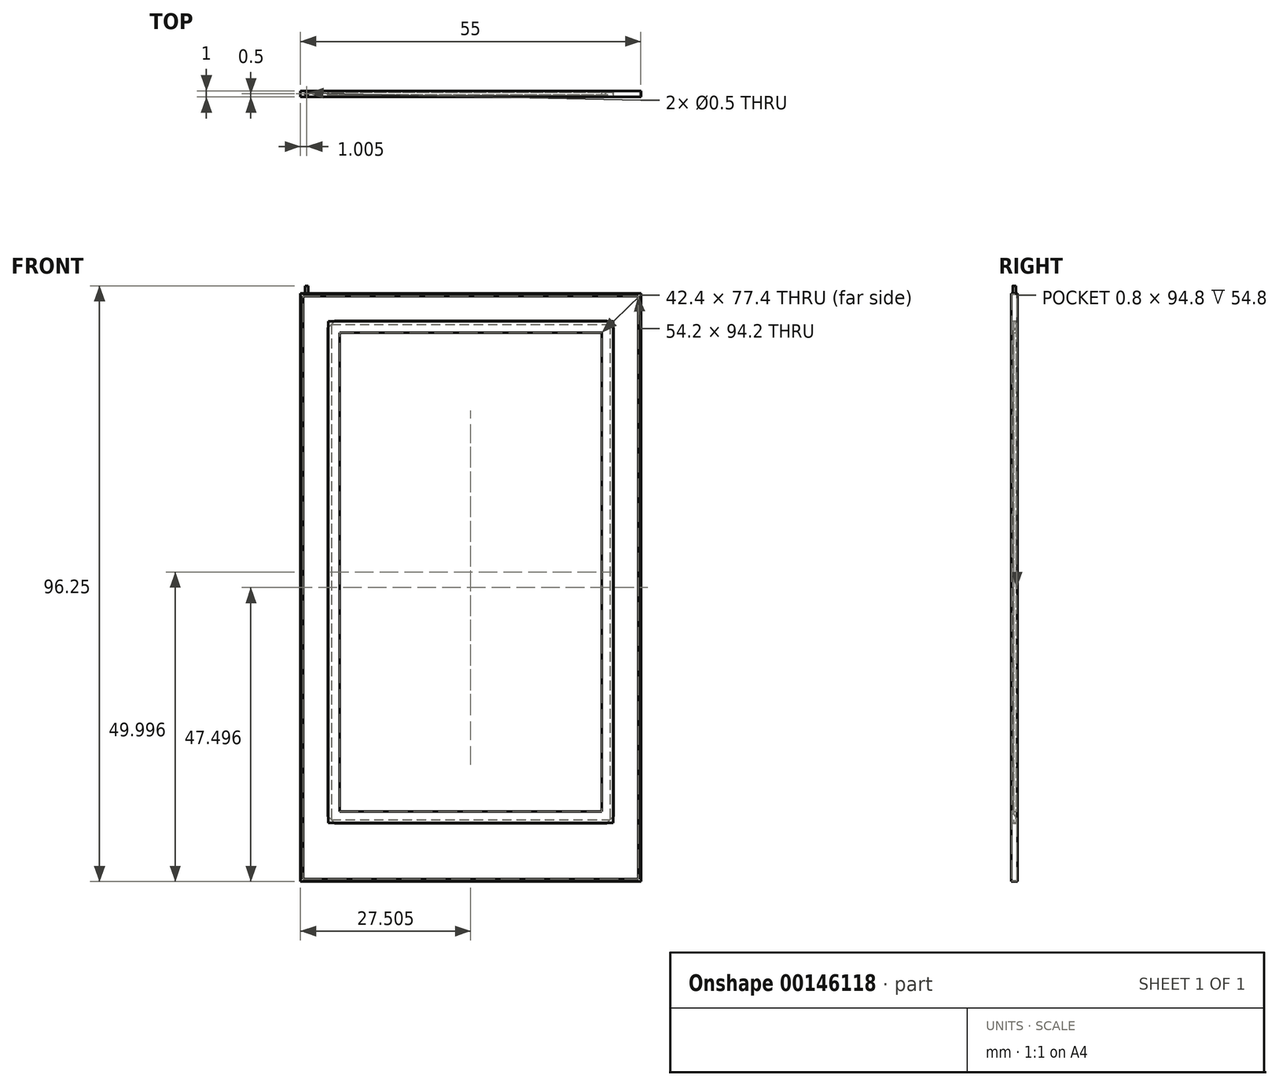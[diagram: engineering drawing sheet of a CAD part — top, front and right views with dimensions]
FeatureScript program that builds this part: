
annotation { "Feature Type Name" : "Feature", "Feature Type Description" : "" }
export const myFeature = defineFeature(function(context is Context, id is Id, definition is map)
    precondition{}
    {
        {
            var Q0;
            Q0=qCreatedBy(makeId("Front.planeOp"),FACE);
            var sketch = newSketch(context, id + "F0", { "sketchPlane" : qUnion([Q0])});
            skLineSegment(sketch, "E0.bottom", {"start": v(-18.52, 34.44) * mm, "end": v(38.48, 34.44) * mm});
            skLineSegment(sketch, "E0.top", {"start": v(-18.52, -62.56) * mm, "end": v(38.48, -62.56) * mm});
            skLineSegment(sketch, "E0.left", {"start": v(-18.52, 34.44) * mm, "end": v(-18.52, -62.56) * mm});
            skLineSegment(sketch, "E0.right", {"start": v(38.48, 34.44) * mm, "end": v(38.48, -62.56) * mm});
            skSolve(sketch);
        }
        {
            var Q0;
            Q0=makeQuery(id+"F0.imprint","IMPRINT",FACE,{"disambiguationData":[TD([[makeQuery(id+"F0.imprint","IMPRINT",EDGE,{"derivedFrom":sQuery(id+"F0.wireOp",EDGE,"E0.bottom")}),-1.0]])]});
            extrude(context, id + "F1", {"entities" : qUnion([Q0]), "depth" : .1 * mm});
        }
        {
            var Q0;
            Q0=makeQuery(id+"F1.opExtrude","CAP_FACE",FACE,{"disambiguationData":[OSD([sQuery(id+"F0.wireOp",EDGE,"E0.bottom"),sQuery(id+"F0.wireOp",EDGE,"E0.top"),sQuery(id+"F0.wireOp",EDGE,"E0.left"),sQuery(id+"F0.wireOp",EDGE,"E0.right")])],"isStart":false});
            var sketch = newSketch(context, id + "F2", { "sketchPlane" : qUnion([Q0])});
            skLineSegment(sketch, "E1.0", {"start": v(-18.22, 34.14) * mm, "end": v(38.18, 34.14) * mm});
            skLineSegment(sketch, "E1.1", {"start": v(-18.22, 34.14) * mm, "end": v(-18.22, -62.26) * mm});
            skLineSegment(sketch, "E1.2", {"start": v(-18.22, -62.26) * mm, "end": v(38.18, -62.26) * mm});
            skLineSegment(sketch, "E1.3", {"start": v(38.18, 34.14) * mm, "end": v(38.18, -62.26) * mm});
            skLineSegment(sketch, "E2.0", {"start": v(-17.52, 33.44) * mm, "end": v(-17.52, -61.56) * mm});
            skLineSegment(sketch, "E2.1", {"start": v(-17.52, 33.44) * mm, "end": v(37.48, 33.44) * mm});
            skLineSegment(sketch, "E2.2", {"start": v(37.48, 33.44) * mm, "end": v(37.48, -61.56) * mm});
            skLineSegment(sketch, "E2.3", {"start": v(-17.52, -61.56) * mm, "end": v(37.48, -61.56) * mm});
            skLineSegment(sketch, "E3", {"start": v(-17.52, 33.44) * mm, "end": v(-17.52, 34.44) * mm});
            skLineSegment(sketch, "E4", {"start": v(-17.52, 33.44) * mm, "end": v(-18.52, 33.44) * mm});
            skLineSegment(sketch, "E5.0", {"start": v(-16.52, 33.44) * mm, "end": v(-16.52, 34.14) * mm, "construction": true});
            skLineSegment(sketch, "E6", {"start": v(37.48, 33.44) * mm, "end": v(37.48, 34.44) * mm});
            skLineSegment(sketch, "E7", {"start": v(37.48, 33.44) * mm, "end": v(38.48, 33.44) * mm});
            skLineSegment(sketch, "E8", {"start": v(37.48, -61.56) * mm, "end": v(37.48, -62.56) * mm});
            skLineSegment(sketch, "E9", {"start": v(37.48, -61.56) * mm, "end": v(38.48, -61.56) * mm});
            skLineSegment(sketch, "E10", {"start": v(-17.52, -61.56) * mm, "end": v(-18.52, -61.56) * mm});
            skLineSegment(sketch, "E11", {"start": v(-17.52, -61.56) * mm, "end": v(-17.52, -62.56) * mm});
            skLineSegment(sketch, "E12", {"start": v(-16.52, -61.56) * mm, "end": v(-16.52, -62.26) * mm, "construction": true});
            skCircle(sketch, "E13", {"center": v(-16.52, -61.91) * mm, "radius": 0.25 * mm});
            skCircle(sketch, "E14", {"center": v(-16.52, 33.79) * mm, "radius": 0.25 * mm});
            skLineSegment(sketch, "E15.0", {"start": v(-17.42, 33.34) * mm, "end": v(37.38, 33.34) * mm});
            skLineSegment(sketch, "E15.1", {"start": v(-17.42, 33.34) * mm, "end": v(-17.42, -61.46) * mm});
            skLineSegment(sketch, "E15.2", {"start": v(-17.42, -61.46) * mm, "end": v(37.38, -61.46) * mm});
            skLineSegment(sketch, "E15.3", {"start": v(37.38, 33.34) * mm, "end": v(37.38, -61.46) * mm});
            skLineSegment(sketch, "E16.0", {"start": v(-17.52, -51.56) * mm, "end": v(-17.42, -51.56) * mm, "construction": true});
            skLineSegment(sketch, "E17.0", {"start": v(-12.52, 33.44) * mm, "end": v(-12.52, 33.34) * mm, "construction": true});
            skLineSegment(sketch, "E18.0", {"start": v(32.48, 33.44) * mm, "end": v(32.48, 33.34) * mm, "construction": true});
            skLineSegment(sketch, "E19.0", {"start": v(-17.52, 28.44) * mm, "end": v(-17.42, 28.44) * mm, "construction": true});
            skLineSegment(sketch, "E20.trimOffspring", {"start": v(-12.52, 28.44) * mm, "end": v(-12.52, -51.56) * mm, "construction": true});
            skLineSegment(sketch, "E21.trimOffspring", {"start": v(-12.52, 28.44) * mm, "end": v(32.48, 28.44) * mm, "construction": true});
            skLineSegment(sketch, "E22.trimOffspring", {"start": v(32.48, 28.44) * mm, "end": v(32.48, -51.56) * mm, "construction": true});
            skLineSegment(sketch, "E23.trimOffspring", {"start": v(37.38, 28.44) * mm, "end": v(37.48, 28.44) * mm, "construction": true});
            skLineSegment(sketch, "E24.trimOffspring", {"start": v(37.38, -51.56) * mm, "end": v(37.48, -51.56) * mm, "construction": true});
            skLineSegment(sketch, "E25.trimOffspring", {"start": v(32.48, -61.46) * mm, "end": v(32.48, -61.56) * mm, "construction": true});
            skLineSegment(sketch, "E26.trimOffspring", {"start": v(-12.52, -61.46) * mm, "end": v(-12.52, -61.56) * mm, "construction": true});
            skLineSegment(sketch, "E27.trimOffspring", {"start": v(-12.52, -51.56) * mm, "end": v(32.48, -51.56) * mm, "construction": true});
            skLineSegment(sketch, "E28.0", {"start": v(32.18, 28.14) * mm, "end": v(32.18, -51.26) * mm, "construction": true});
            skLineSegment(sketch, "E28.1", {"start": v(-12.22, 28.14) * mm, "end": v(32.18, 28.14) * mm, "construction": true});
            skLineSegment(sketch, "E28.2", {"start": v(-12.22, 28.14) * mm, "end": v(-12.22, -51.26) * mm, "construction": true});
            skLineSegment(sketch, "E28.3", {"start": v(-12.22, -51.26) * mm, "end": v(32.18, -51.26) * mm, "construction": true});
            skLineSegment(sketch, "E29.0", {"start": v(-11.72, 27.64) * mm, "end": v(-11.72, -50.76) * mm, "construction": true});
            skLineSegment(sketch, "E29.1", {"start": v(-11.72, 27.64) * mm, "end": v(31.68, 27.64) * mm, "construction": true});
            skLineSegment(sketch, "E29.2", {"start": v(31.68, 27.64) * mm, "end": v(31.68, -50.76) * mm, "construction": true});
            skLineSegment(sketch, "E29.3", {"start": v(-11.72, -50.76) * mm, "end": v(31.68, -50.76) * mm, "construction": true});
            skLineSegment(sketch, "E30.0", {"start": v(-11.22, 27.14) * mm, "end": v(31.18, 27.14) * mm});
            skLineSegment(sketch, "E30.1", {"start": v(-11.22, 27.14) * mm, "end": v(-11.22, -50.26) * mm});
            skLineSegment(sketch, "E30.2", {"start": v(-11.22, -50.26) * mm, "end": v(31.18, -50.26) * mm});
            skLineSegment(sketch, "E30.3", {"start": v(31.18, 27.14) * mm, "end": v(31.18, -50.26) * mm});
            skSolve(sketch);
        }
        {
            var Q0;
            Q0=makeQuery(id+"F2.imprint","IMPRINT",FACE,{"disambiguationData":[TD([[makeQuery(id+"F2.imprint","IMPRINT",EDGE,{"derivedFrom":sQuery(id+"F2.wireOp",EDGE,"E14")}),1.0]])]});
            var Q1;
            Q1=makeQuery(id+"F2.imprint","IMPRINT",FACE,{"disambiguationData":[TD([[makeQuery(id+"F2.imprint","IMPRINT",EDGE,{"derivedFrom":sQuery(id+"F2.wireOp",EDGE,"E13")}),1.0]])]});
            var Q2;
            {var subQ0=sQuery(id+"F2.wireOp",EDGE,"E1.2");var subQ1=sQuery(id+"F2.wireOp",EDGE,"E1.1");var subQ2=makeQuery(id+"F2.imprint","INTERSECT",VERTEX,{"derivedFrom":[subQ1,subQ0]});Q2=makeQuery(id+"F2.imprint","IMPRINT",FACE,{"disambiguationData":[TD([[makeQuery(id+"F2.imprint","IMPRINT",EDGE,{"disambiguationData":[TD([[subQ2,1.0]])],"derivedFrom":subQ1}),1.0]])]});}
            var Q3;
            {var subQ3=sQuery(id+"F2.wireOp",EDGE,"E1.2");var subQ8=sQuery(id+"F2.wireOp",EDGE,"E1.1");var subQ10=makeQuery(id+"F2.imprint","INTERSECT",VERTEX,{"derivedFrom":[subQ8,subQ3]});Q3=makeQuery(id+"F2.imprint","IMPRINT",FACE,{"disambiguationData":[TD([[makeQuery(id+"F2.imprint","IMPRINT",EDGE,{"disambiguationData":[TD([[subQ10,1.0]])],"derivedFrom":subQ8}),-1.0]])]});}
            var Q4;
            {var subQ3=sQuery(id+"F2.wireOp",EDGE,"E1.1");var subQ5=sQuery(id+"F2.wireOp",EDGE,"E1.0");var subQ6=makeQuery(id+"F2.imprint","INTERSECT",VERTEX,{"derivedFrom":[subQ5,subQ3]});Q4=makeQuery(id+"F2.imprint","IMPRINT",FACE,{"disambiguationData":[TD([[makeQuery(id+"F2.imprint","IMPRINT",EDGE,{"disambiguationData":[TD([[subQ6,-1.0]])],"derivedFrom":subQ5}),1.0]])]});}
            var Q5;
            {var subQ0=sQuery(id+"F2.wireOp",EDGE,"E1.1");var subQ1=sQuery(id+"F2.wireOp",EDGE,"E1.0");var subQ2=makeQuery(id+"F2.imprint","INTERSECT",VERTEX,{"derivedFrom":[subQ1,subQ0]});Q5=makeQuery(id+"F2.imprint","IMPRINT",FACE,{"disambiguationData":[TD([[makeQuery(id+"F2.imprint","IMPRINT",EDGE,{"disambiguationData":[TD([[subQ2,-1.0]])],"derivedFrom":subQ1}),-1.0]])]});}
            var Q6;
            {var subQ3=sQuery(id+"F2.wireOp",EDGE,"E1.3");var subQ8=sQuery(id+"F2.wireOp",EDGE,"E1.0");var subQ10=makeQuery(id+"F2.imprint","INTERSECT",VERTEX,{"derivedFrom":[subQ8,subQ3]});Q6=makeQuery(id+"F2.imprint","IMPRINT",FACE,{"disambiguationData":[TD([[makeQuery(id+"F2.imprint","IMPRINT",EDGE,{"disambiguationData":[TD([[subQ10,1.0]])],"derivedFrom":subQ8}),1.0]])]});}
            var Q7;
            {var subQ0=sQuery(id+"F2.wireOp",EDGE,"E1.3");var subQ1=sQuery(id+"F2.wireOp",EDGE,"E1.0");var subQ2=makeQuery(id+"F2.imprint","INTERSECT",VERTEX,{"derivedFrom":[subQ1,subQ0]});Q7=makeQuery(id+"F2.imprint","IMPRINT",FACE,{"disambiguationData":[TD([[makeQuery(id+"F2.imprint","IMPRINT",EDGE,{"disambiguationData":[TD([[subQ2,1.0]])],"derivedFrom":subQ1}),-1.0]])]});}
            var Q8;
            {var subQ3=sQuery(id+"F2.wireOp",EDGE,"E1.3");var subQ5=sQuery(id+"F2.wireOp",EDGE,"E1.2");var subQ6=makeQuery(id+"F2.imprint","INTERSECT",VERTEX,{"derivedFrom":[subQ5,subQ3]});Q8=makeQuery(id+"F2.imprint","IMPRINT",FACE,{"disambiguationData":[TD([[makeQuery(id+"F2.imprint","IMPRINT",EDGE,{"disambiguationData":[TD([[subQ6,1.0]])],"derivedFrom":subQ5}),-1.0]])]});}
            var Q9;
            {var subQ0=sQuery(id+"F2.wireOp",EDGE,"E1.3");var subQ1=sQuery(id+"F2.wireOp",EDGE,"E1.2");var subQ2=makeQuery(id+"F2.imprint","INTERSECT",VERTEX,{"derivedFrom":[subQ1,subQ0]});Q9=makeQuery(id+"F2.imprint","IMPRINT",FACE,{"disambiguationData":[TD([[makeQuery(id+"F2.imprint","IMPRINT",EDGE,{"disambiguationData":[TD([[subQ2,1.0]])],"derivedFrom":subQ1}),1.0]])]});}
            var Q10;
            Q10=makeQuery(id+"F2.imprint","IMPRINT",FACE,{"disambiguationData":[TD([[makeQuery(id+"F2.imprint","IMPRINT",EDGE,{"derivedFrom":sQuery(id+"F2.wireOp",EDGE,"E30.0")}),-1.0]])]});
            extrude(context, id + "F3", {"entities" : qUnion([Q0, Q1, Q2, Q3, Q4, Q5, Q6, Q7, Q8, Q9, Q10]), "operationType" : NewBodyOperationType.REMOVE, "oppositeDirection" : true, "depth" : 25 * mm});
        }
        {
            var Q0;
            Q0=makeQuery(id+"F2.imprint","IMPRINT",FACE,{"disambiguationData":[TD([[makeQuery(id+"F2.imprint","IMPRINT",EDGE,{"derivedFrom":sQuery(id+"F2.wireOp",EDGE,"E2.0")}),1.0]])]});
            extrude(context, id + "F4", {"entities" : qUnion([Q0]), "operationType" : NewBodyOperationType.ADD, "depth" : 0.8 * mm});
        }
        {
            var Q0;
            Q0=makeQuery(id+"F4.opExtrude","SWEPT_FACE",FACE,{"disambiguationData":[OSD([sQuery(id+"F2.wireOp",EDGE,"E2.1")])]});
            var sketch = newSketch(context, id + "F5", { "sketchPlane" : qUnion([Q0])});
            skLineSegment(sketch, "E31.0", {"start": v(-16.52, -0.9) * mm, "end": v(-16.52, -0.1) * mm, "construction": true});
            skCircle(sketch, "E32", {"center": v(-16.52, -0.5) * mm, "radius": 0.25 * mm});
            skSolve(sketch);
        }
        {
            var Q0;
            Q0=makeQuery(id+"F5.imprint","IMPRINT",FACE,{"disambiguationData":[TD([[makeQuery(id+"F5.imprint","IMPRINT",EDGE,{"derivedFrom":sQuery(id+"F5.wireOp",EDGE,"E32")}),1.0]])]});
            extrude(context, id + "F6", {"entities" : qUnion([Q0]), "operationType" : NewBodyOperationType.REMOVE, "oppositeDirection" : true, "depth" : 100 * mm});
        }
        {
            var Q0;
            {var subQ0=sQuery(id+"F0.wireOp",EDGE,"E0.left");var subQ1=makeQuery(id+"F1.opExtrude","CAP_FACE",FACE,{"disambiguationData":[OSD([sQuery(id+"F0.wireOp",EDGE,"E0.bottom"),sQuery(id+"F0.wireOp",EDGE,"E0.top"),subQ0,sQuery(id+"F0.wireOp",EDGE,"E0.right")])],"isStart":false});Q0=makeQuery(id+"F4.boolean.opBoolean","SPLIT",FACE,{"disambiguationData":[TD([makeQuery(id+"F1.opExtrude","SWEPT_FACE",FACE,{"disambiguationData":[OSD([subQ0])]})])],"derivedFrom":subQ1});}
            var Q1;
            {var subQ0=sQuery(id+"F0.wireOp",EDGE,"E0.bottom");var subQ1=makeQuery(id+"F1.opExtrude","CAP_FACE",FACE,{"disambiguationData":[OSD([subQ0,sQuery(id+"F0.wireOp",EDGE,"E0.top"),sQuery(id+"F0.wireOp",EDGE,"E0.left"),sQuery(id+"F0.wireOp",EDGE,"E0.right")])],"isStart":false});Q1=makeQuery(id+"F4.boolean.opBoolean","SPLIT",FACE,{"disambiguationData":[TD([makeQuery(id+"F1.opExtrude","SWEPT_FACE",FACE,{"disambiguationData":[OSD([subQ0])]})])],"derivedFrom":subQ1});}
            var Q2;
            {var subQ0=sQuery(id+"F0.wireOp",EDGE,"E0.right");var subQ1=makeQuery(id+"F1.opExtrude","CAP_FACE",FACE,{"disambiguationData":[OSD([sQuery(id+"F0.wireOp",EDGE,"E0.bottom"),sQuery(id+"F0.wireOp",EDGE,"E0.top"),sQuery(id+"F0.wireOp",EDGE,"E0.left"),subQ0])],"isStart":false});Q2=makeQuery(id+"F4.boolean.opBoolean","SPLIT",FACE,{"disambiguationData":[TD([makeQuery(id+"F1.opExtrude","SWEPT_FACE",FACE,{"disambiguationData":[OSD([subQ0])]})])],"derivedFrom":subQ1});}
            var Q3;
            {var subQ0=sQuery(id+"F0.wireOp",EDGE,"E0.top");var subQ1=makeQuery(id+"F1.opExtrude","CAP_FACE",FACE,{"disambiguationData":[OSD([sQuery(id+"F0.wireOp",EDGE,"E0.bottom"),subQ0,sQuery(id+"F0.wireOp",EDGE,"E0.left"),sQuery(id+"F0.wireOp",EDGE,"E0.right")])],"isStart":false});Q3=makeQuery(id+"F4.boolean.opBoolean","SPLIT",FACE,{"disambiguationData":[TD([makeQuery(id+"F1.opExtrude","SWEPT_FACE",FACE,{"disambiguationData":[OSD([subQ0])]})])],"derivedFrom":subQ1});}
            extrude(context, id + "F7", {"entities" : qUnion([Q0, Q1, Q2, Q3]), "operationType" : NewBodyOperationType.REMOVE, "oppositeDirection" : true, "depth" : 25 * mm});
        }
        {
            var Q0;
            Q0=makeQuery(id+"F4.opExtrude","CAP_FACE",FACE,{"disambiguationData":[OSD([sQuery(id+"F2.wireOp",EDGE,"E2.0"),sQuery(id+"F2.wireOp",EDGE,"E2.1"),sQuery(id+"F2.wireOp",EDGE,"E2.2"),sQuery(id+"F2.wireOp",EDGE,"E2.3"),sQuery(id+"F2.wireOp",EDGE,"E15.0"),sQuery(id+"F2.wireOp",EDGE,"E15.1"),sQuery(id+"F2.wireOp",EDGE,"E15.2"),sQuery(id+"F2.wireOp",EDGE,"E15.3")])],"isStart":false});
            var sketch = newSketch(context, id + "F8", { "sketchPlane" : qUnion([Q0])});
            skLineSegment(sketch, "E33.0", {"start": v(-17.12, 33.04) * mm, "end": v(37.08, 33.04) * mm});
            skLineSegment(sketch, "E33.1", {"start": v(-17.12, 33.04) * mm, "end": v(-17.12, -61.16) * mm});
            skLineSegment(sketch, "E33.2", {"start": v(-17.12, -61.16) * mm, "end": v(37.08, -61.16) * mm});
            skLineSegment(sketch, "E33.3", {"start": v(37.08, 33.04) * mm, "end": v(37.08, -61.16) * mm});
            skSolve(sketch);
        }
        {
            var Q0;
            Q0=makeQuery(id+"F8.imprint","IMPRINT",FACE,{"disambiguationData":[TD([[makeQuery(id+"F8.imprint","IMPRINT",EDGE,{"derivedFrom":sQuery(id+"F8.wireOp",EDGE,"E33.0")}),1.0]])]});
            var Q1;
            Q1=makeQuery(id+"F8.imprint","IMPRINT",FACE,{"disambiguationData":[TD([[makeQuery(id+"F8.imprint","IMPRINT",EDGE,{"derivedFrom":makeQuery(id+"F4.opExtrude","CAP_EDGE",EDGE,{"disambiguationData":[OSD([sQuery(id+"F2.wireOp",EDGE,"E2.0")])],"isStart":false})}),1.0]])]});
            extrude(context, id + "F9", {"entities" : qUnion([Q0, Q1]), "operationType" : NewBodyOperationType.ADD, "depth" : .1 * mm});
        }
        {
            var Q0;
            Q0=makeQuery(id+"F4.boolean.opBoolean","SPLIT",FACE,{"disambiguationData":[TD([makeQuery(id+"F3.boolean.opBoolean","COPY",FACE,{"derivedFrom":makeQuery(id+"F3.opExtrude","SWEPT_FACE",FACE,{"disambiguationData":[OSD([sQuery(id+"F2.wireOp",EDGE,"E30.0")])]})})])],"derivedFrom":makeQuery(id+"F1.opExtrude","CAP_FACE",FACE,{"disambiguationData":[OSD([sQuery(id+"F0.wireOp",EDGE,"E0.bottom"),sQuery(id+"F0.wireOp",EDGE,"E0.top"),sQuery(id+"F0.wireOp",EDGE,"E0.left"),sQuery(id+"F0.wireOp",EDGE,"E0.right")])],"isStart":false})});
            var sketch = newSketch(context, id + "F10", { "sketchPlane" : qUnion([Q0])});
            skLineSegment(sketch, "E34.0", {"start": v(-12.52, 28.44) * mm, "end": v(32.48, 28.44) * mm});
            skLineSegment(sketch, "E34.1", {"start": v(-12.52, 28.44) * mm, "end": v(-12.52, -51.56) * mm});
            skLineSegment(sketch, "E34.2", {"start": v(32.48, 28.44) * mm, "end": v(32.48, -51.56) * mm});
            skLineSegment(sketch, "E34.3", {"start": v(-12.52, -51.56) * mm, "end": v(32.48, -51.56) * mm});
            skLineSegment(sketch, "E35.0", {"start": v(-12.62, -51.66) * mm, "end": v(32.58, -51.66) * mm});
            skLineSegment(sketch, "E35.1", {"start": v(-12.62, 28.54) * mm, "end": v(-12.62, -51.66) * mm});
            skLineSegment(sketch, "E35.2", {"start": v(-12.62, 28.54) * mm, "end": v(32.58, 28.54) * mm});
            skLineSegment(sketch, "E35.3", {"start": v(32.58, 28.54) * mm, "end": v(32.58, -51.66) * mm});
            skLineSegment(sketch, "E36.0", {"start": v(-13.02, 28.94) * mm, "end": v(-13.02, -52.06) * mm});
            skLineSegment(sketch, "E36.1", {"start": v(-13.02, 28.94) * mm, "end": v(32.98, 28.94) * mm});
            skLineSegment(sketch, "E36.2", {"start": v(32.98, 28.94) * mm, "end": v(32.98, -52.06) * mm});
            skLineSegment(sketch, "E36.3", {"start": v(-13.02, -52.06) * mm, "end": v(32.98, -52.06) * mm});
            skLineSegment(sketch, "E37.0", {"start": v(-13.12, 29.04) * mm, "end": v(-13.12, -52.16) * mm});
            skLineSegment(sketch, "E37.1", {"start": v(-13.12, 29.04) * mm, "end": v(33.08, 29.04) * mm});
            skLineSegment(sketch, "E37.2", {"start": v(33.08, 29.04) * mm, "end": v(33.08, -52.16) * mm});
            skLineSegment(sketch, "E37.3", {"start": v(-13.12, -52.16) * mm, "end": v(33.08, -52.16) * mm});
            skLineSegment(sketch, "E38", {"start": v(-12.52, -51.56) * mm, "end": v(-13.02, -51.06) * mm});
            skLineSegment(sketch, "E39", {"start": v(-12.52, -51.56) * mm, "end": v(-12.02, -52.06) * mm});
            skLineSegment(sketch, "E40", {"start": v(-12.02, -52.06) * mm, "end": v(-12.02, -52.16) * mm});
            skLineSegment(sketch, "E41", {"start": v(-13.02, -51.06) * mm, "end": v(-13.12, -51.06) * mm});
            skLineSegment(sketch, "E42", {"start": v(-12.52, 28.44) * mm, "end": v(-12.02, 28.94) * mm});
            skLineSegment(sketch, "E43", {"start": v(-12.52, 28.44) * mm, "end": v(-13.02, 27.94) * mm});
            skLineSegment(sketch, "E44", {"start": v(-13.02, 27.94) * mm, "end": v(-13.12, 27.94) * mm});
            skLineSegment(sketch, "E45", {"start": v(-12.02, 28.94) * mm, "end": v(-12.02, 29.04) * mm});
            skLineSegment(sketch, "E46", {"start": v(32.48, 28.44) * mm, "end": v(31.98, 28.94) * mm});
            skLineSegment(sketch, "E47", {"start": v(32.48, 28.44) * mm, "end": v(32.98, 27.94) * mm});
            skLineSegment(sketch, "E48", {"start": v(32.98, 27.94) * mm, "end": v(33.08, 27.94) * mm});
            skLineSegment(sketch, "E49", {"start": v(31.98, 28.94) * mm, "end": v(31.98, 29.04) * mm});
            skLineSegment(sketch, "E50", {"start": v(32.48, -51.56) * mm, "end": v(31.98, -52.06) * mm});
            skLineSegment(sketch, "E51", {"start": v(31.98, -52.06) * mm, "end": v(31.98, -52.16) * mm});
            skLineSegment(sketch, "E52", {"start": v(32.48, -51.56) * mm, "end": v(32.98, -51.06) * mm});
            skLineSegment(sketch, "E53", {"start": v(32.98, -51.06) * mm, "end": v(33.08, -51.06) * mm});
            skSolve(sketch);
        }
        {
            var Q0;
            Q0=makeQuery(id+"F10.imprint","IMPRINT",FACE,{"disambiguationData":[TD([[makeQuery(id+"F10.imprint","IMPRINT",EDGE,{"derivedFrom":sQuery(id+"F10.wireOp",EDGE,"E34.0")}),-1.0]])]});
            extrude(context, id + "F11", {"entities" : qUnion([Q0]), "operationType" : NewBodyOperationType.REMOVE, "oppositeDirection" : true, "depth" : 25 * mm});
        }
        {
            var Q0;
            {var subQ0=sQuery(id+"F10.wireOp",EDGE,"E34.1");Q0=makeQuery(id+"F11.boolean.opBoolean","MERGE",FACE,{"derivedFrom":[makeQuery(id+"F1nm8Pht3K346aE_1.opExtrude","SWEPT_FACE",FACE,{"disambiguationData":[OSD([subQ0])]}),makeQuery(id+"F11.opExtrude","SWEPT_FACE",FACE,{"disambiguationData":[OSD([subQ0])]})]});}
            var sketch = newSketch(context, id + "F12", { "sketchPlane" : qUnion([Q0])});
            skLineSegment(sketch, "E54.0", {"start": v(-0.1, 28.54) * mm, "end": v(-0.1, -51.66) * mm});
            skLineSegment(sketch, "E55", {"start": v(-0.1, 28.44) * mm, "end": v(-0.6, 27.94) * mm});
            skSolve(sketch);
        }
        {
            var Q0;
            {var subQ0=sQuery(id+"F10.wireOp",EDGE,"E34.0");Q0=makeQuery(id+"FM4QFzq4VBppDcW_1.boolean.opBoolean","MERGE",FACE,{"derivedFrom":[makeQuery(id+"F11.boolean.opBoolean","MERGE",FACE,{"derivedFrom":[makeQuery(id+"F1nm8Pht3K346aE_1.opExtrude","SWEPT_FACE",FACE,{"disambiguationData":[OSD([subQ0])]}),makeQuery(id+"F11.opExtrude","SWEPT_FACE",FACE,{"disambiguationData":[OSD([subQ0])]})]}),makeQuery(id+"FM4QFzq4VBppDcW_1.opExtrude","SWEPT_FACE",FACE,{"disambiguationData":[OSD([subQ0,sQuery(id+"F10.wireOp",EDGE,"E34.1")])]})]});}
            var sketch = newSketch(context, id + "F13", { "sketchPlane" : qUnion([Q0])});
            skLineSegment(sketch, "E56", {"start": v(-12.52, 0.1) * mm, "end": v(-12.02, 0.6) * mm});
            skSolve(sketch);
        }
        {
            var Q0;
            {var subQ0=sQuery(id+"F10.wireOp",EDGE,"E40");Q0=makeQuery(id+"F10.imprint","IMPRINT",FACE,{"disambiguationData":[TD([[makeQuery(id+"F10.imprint","IMPRINT",EDGE,{"derivedFrom":subQ0}),1.0]])]});}
            var Q1;
            {var subQ0=sQuery(id+"F10.wireOp",EDGE,"E48");Q1=makeQuery(id+"F10.imprint","IMPRINT",FACE,{"disambiguationData":[TD([[makeQuery(id+"F10.imprint","IMPRINT",EDGE,{"derivedFrom":subQ0}),-1.0]])]});}
            var Q2;
            {var subQ0=sQuery(id+"F10.wireOp",EDGE,"E41");Q2=makeQuery(id+"F10.imprint","IMPRINT",FACE,{"disambiguationData":[TD([[makeQuery(id+"F10.imprint","IMPRINT",EDGE,{"derivedFrom":subQ0}),-1.0]])]});}
            var Q3;
            {var subQ0=sQuery(id+"F10.wireOp",EDGE,"E45");Q3=makeQuery(id+"F10.imprint","IMPRINT",FACE,{"disambiguationData":[TD([[makeQuery(id+"F10.imprint","IMPRINT",EDGE,{"derivedFrom":subQ0}),-1.0]])]});}
            extrude(context, id + "F14", {"entities" : qUnion([Q0, Q1, Q2, Q3]), "operationType" : NewBodyOperationType.ADD, "depth" : .6 * mm});
        }
        {
            var Q0;
            {var subQ0=sQuery(id+"F10.wireOp",EDGE,"E34.0");Q0=makeQuery(id+"F10.imprint","IMPRINT",FACE,{"disambiguationData":[TD([[makeQuery(id+"F10.imprint","IMPRINT",EDGE,{"derivedFrom":subQ0}),1.0]])]});}
            var Q1;
            {var subQ0=sQuery(id+"F10.wireOp",EDGE,"E42");var subQ1=sQuery(id+"F10.wireOp",EDGE,"E35.2");var subQ2=makeQuery(id+"F10.imprint","INTERSECT",VERTEX,{"derivedFrom":[subQ1,subQ0]});Q1=makeQuery(id+"F10.imprint","IMPRINT",FACE,{"disambiguationData":[TD([[makeQuery(id+"F10.imprint","IMPRINT",EDGE,{"disambiguationData":[TD([[subQ2,-1.0]])],"derivedFrom":subQ1}),1.0]])]});}
            var Q2;
            {var subQ0=sQuery(id+"F10.wireOp",EDGE,"E47");var subQ1=sQuery(id+"F10.wireOp",EDGE,"E35.3");var subQ2=makeQuery(id+"F10.imprint","INTERSECT",VERTEX,{"derivedFrom":[subQ1,subQ0]});Q2=makeQuery(id+"F10.imprint","IMPRINT",FACE,{"disambiguationData":[TD([[makeQuery(id+"F10.imprint","IMPRINT",EDGE,{"disambiguationData":[TD([[subQ2,-1.0]])],"derivedFrom":subQ1}),1.0]])]});}
            var Q3;
            {var subQ0=sQuery(id+"F10.wireOp",EDGE,"E43");var subQ1=sQuery(id+"F10.wireOp",EDGE,"E35.1");var subQ2=makeQuery(id+"F10.imprint","INTERSECT",VERTEX,{"derivedFrom":[subQ1,subQ0]});Q3=makeQuery(id+"F10.imprint","IMPRINT",FACE,{"disambiguationData":[TD([[makeQuery(id+"F10.imprint","IMPRINT",EDGE,{"disambiguationData":[TD([[subQ2,-1.0]])],"derivedFrom":subQ1}),-1.0]])]});}
            var Q4;
            {var subQ0=sQuery(id+"F10.wireOp",EDGE,"E39");var subQ1=sQuery(id+"F10.wireOp",EDGE,"E35.0");var subQ2=makeQuery(id+"F10.imprint","INTERSECT",VERTEX,{"derivedFrom":[subQ1,subQ0]});Q4=makeQuery(id+"F10.imprint","IMPRINT",FACE,{"disambiguationData":[TD([[makeQuery(id+"F10.imprint","IMPRINT",EDGE,{"disambiguationData":[TD([[subQ2,-1.0]])],"derivedFrom":subQ1}),-1.0]])]});}
            var Q5;
            {var subQ0=sQuery(id+"F10.wireOp",EDGE,"E34.3");Q5=makeQuery(id+"F10.imprint","IMPRINT",FACE,{"disambiguationData":[TD([[makeQuery(id+"F10.imprint","IMPRINT",EDGE,{"derivedFrom":subQ0}),-1.0]])]});}
            extrude(context, id + "F15", {"entities" : qUnion([Q0, Q1, Q2, Q3, Q4, Q5]), "operationType" : NewBodyOperationType.ADD, "depth" : .1 * mm});
        }
        {
            var Q0;
            Q0=makeQuery(id+"F15.opExtrude","SWEPT_FACE",FACE,{"disambiguationData":[OSD([sQuery(id+"F10.wireOp",EDGE,"E35.1")])]});
            extrude(context, id + "F16", {"entities" : qUnion([Q0]), "operationType" : NewBodyOperationType.ADD, "depth" : .1 * mm});
        }
        {
            var Q0;
            Q0=makeQuery(id+"F15.opExtrude","SWEPT_FACE",FACE,{"disambiguationData":[OSD([sQuery(id+"F10.wireOp",EDGE,"E35.3")])]});
            extrude(context, id + "F17", {"entities" : qUnion([Q0]), "operationType" : NewBodyOperationType.ADD, "depth" : .1 * mm});
        }
        {
            var Q0;
            Q0=makeQuery(id+"F14.opExtrude","CAP_EDGE",EDGE,{"disambiguationData":[OSD([sQuery(id+"F10.wireOp",EDGE,"E53")])],"isStart":false});
            var Q1;
            Q1=makeQuery(id+"F14.opExtrude","CAP_EDGE",EDGE,{"disambiguationData":[OSD([sQuery(id+"F10.wireOp",EDGE,"E51")])],"isStart":false});
            var Q2;
            Q2=makeQuery(id+"F14.opExtrude","CAP_EDGE",EDGE,{"disambiguationData":[OSD([sQuery(id+"F10.wireOp",EDGE,"E41")])],"isStart":false});
            var Q3;
            Q3=makeQuery(id+"F14.opExtrude","CAP_EDGE",EDGE,{"disambiguationData":[OSD([sQuery(id+"F10.wireOp",EDGE,"E40")])],"isStart":false});
            var Q4;
            Q4=makeQuery(id+"F14.opExtrude","CAP_EDGE",EDGE,{"disambiguationData":[OSD([sQuery(id+"F10.wireOp",EDGE,"E45")])],"isStart":false});
            var Q5;
            Q5=makeQuery(id+"F14.opExtrude","CAP_EDGE",EDGE,{"disambiguationData":[OSD([sQuery(id+"F10.wireOp",EDGE,"E44")])],"isStart":false});
            var Q6;
            Q6=makeQuery(id+"F14.opExtrude","CAP_EDGE",EDGE,{"disambiguationData":[OSD([sQuery(id+"F10.wireOp",EDGE,"E49")])],"isStart":false});
            var Q7;
            Q7=makeQuery(id+"F14.opExtrude","CAP_EDGE",EDGE,{"disambiguationData":[OSD([sQuery(id+"F10.wireOp",EDGE,"E48")])],"isStart":false});
            chamfer(context, id + "F18", {"entities" : qUnion([Q0, Q1, Q2, Q3, Q4, Q5, Q6, Q7]), "width" : .5 * mm, "tangentPropagation" : true});
        }
        {
            var Q0;
            {var subQ7=sQuery(id+"F10.wireOp",EDGE,"E35.2");var subQ8=sQuery(id+"F10.wireOp",EDGE,"E35.1");var subQ9=makeQuery(id+"F10.imprint","INTERSECT",VERTEX,{"derivedFrom":[subQ8,subQ7]});Q0=makeQuery(id+"F10.imprint","IMPRINT",FACE,{"disambiguationData":[TD([[makeQuery(id+"F10.imprint","IMPRINT",EDGE,{"disambiguationData":[TD([[subQ9,-1.0]])],"derivedFrom":subQ8}),-1.0]])]});}
            var Q1;
            {var subQ0=sQuery(id+"F10.wireOp",EDGE,"E35.2");var subQ1=sQuery(id+"F10.wireOp",EDGE,"E35.1");var subQ2=makeQuery(id+"F10.imprint","INTERSECT",VERTEX,{"derivedFrom":[subQ1,subQ0]});Q1=makeQuery(id+"F10.imprint","IMPRINT",FACE,{"disambiguationData":[TD([[makeQuery(id+"F10.imprint","IMPRINT",EDGE,{"disambiguationData":[TD([[subQ2,-1.0]])],"derivedFrom":subQ1}),1.0]])]});}
            var Q2;
            {var subQ0=sQuery(id+"F10.wireOp",EDGE,"E42");var subQ1=sQuery(id+"F10.wireOp",EDGE,"E35.2");var subQ2=makeQuery(id+"F10.imprint","INTERSECT",VERTEX,{"derivedFrom":[subQ1,subQ0]});Q2=makeQuery(id+"F10.imprint","IMPRINT",FACE,{"disambiguationData":[TD([[makeQuery(id+"F10.imprint","IMPRINT",EDGE,{"disambiguationData":[TD([[subQ2,-1.0]])],"derivedFrom":subQ1}),1.0]])]});}
            var Q3;
            {var subQ0=sQuery(id+"F10.wireOp",EDGE,"E43");var subQ1=sQuery(id+"F10.wireOp",EDGE,"E35.1");var subQ2=makeQuery(id+"F10.imprint","INTERSECT",VERTEX,{"derivedFrom":[subQ1,subQ0]});Q3=makeQuery(id+"F10.imprint","IMPRINT",FACE,{"disambiguationData":[TD([[makeQuery(id+"F10.imprint","IMPRINT",EDGE,{"disambiguationData":[TD([[subQ2,-1.0]])],"derivedFrom":subQ1}),-1.0]])]});}
            var Q4;
            {var subQ0=sQuery(id+"F10.wireOp",EDGE,"E34.0");Q4=makeQuery(id+"F10.imprint","IMPRINT",FACE,{"disambiguationData":[TD([[makeQuery(id+"F10.imprint","IMPRINT",EDGE,{"derivedFrom":subQ0}),1.0]])]});}
            var Q5;
            {var subQ0=sQuery(id+"F10.wireOp",EDGE,"E34.1");Q5=makeQuery(id+"F10.imprint","IMPRINT",FACE,{"disambiguationData":[TD([[makeQuery(id+"F10.imprint","IMPRINT",EDGE,{"derivedFrom":subQ0}),-1.0]])]});}
            var Q6;
            Q6=makeQuery(id+"F10.imprint","IMPRINT",FACE,{"disambiguationData":[TD([[makeQuery(id+"F10.imprint","IMPRINT",EDGE,{"derivedFrom":sQuery(id+"F10.wireOp",EDGE,"E34.0")}),-1.0]])]});
            var Q7;
            Q7=makeQuery(id+"F10.imprint","IMPRINT",FACE,{"disambiguationData":[TD([[makeQuery(id+"F10.imprint","IMPRINT",EDGE,{"derivedFrom":makeQuery(id+"F3.boolean.opBoolean","COPY",EDGE,{"derivedFrom":makeQuery(id+"F3.opExtrude","CAP_EDGE",EDGE,{"disambiguationData":[OSD([sQuery(id+"F2.wireOp",EDGE,"E30.0")])],"isStart":true})})}),-1.0]])]});
            var Q8;
            {var subQ7=sQuery(id+"F10.wireOp",EDGE,"E35.3");var subQ8=sQuery(id+"F10.wireOp",EDGE,"E35.2");var subQ9=makeQuery(id+"F10.imprint","INTERSECT",VERTEX,{"derivedFrom":[subQ8,subQ7]});Q8=makeQuery(id+"F10.imprint","IMPRINT",FACE,{"disambiguationData":[TD([[makeQuery(id+"F10.imprint","IMPRINT",EDGE,{"disambiguationData":[TD([[subQ9,1.0]])],"derivedFrom":subQ8}),1.0]])]});}
            var Q9;
            {var subQ0=sQuery(id+"F10.wireOp",EDGE,"E35.3");var subQ1=sQuery(id+"F10.wireOp",EDGE,"E35.2");var subQ2=makeQuery(id+"F10.imprint","INTERSECT",VERTEX,{"derivedFrom":[subQ1,subQ0]});Q9=makeQuery(id+"F10.imprint","IMPRINT",FACE,{"disambiguationData":[TD([[makeQuery(id+"F10.imprint","IMPRINT",EDGE,{"disambiguationData":[TD([[subQ2,1.0]])],"derivedFrom":subQ1}),-1.0]])]});}
            var Q10;
            {var subQ0=sQuery(id+"F10.wireOp",EDGE,"E34.2");Q10=makeQuery(id+"F10.imprint","IMPRINT",FACE,{"disambiguationData":[TD([[makeQuery(id+"F10.imprint","IMPRINT",EDGE,{"derivedFrom":subQ0}),1.0]])]});}
            var Q11;
            {var subQ0=sQuery(id+"F10.wireOp",EDGE,"E47");var subQ1=sQuery(id+"F10.wireOp",EDGE,"E35.3");var subQ2=makeQuery(id+"F10.imprint","INTERSECT",VERTEX,{"derivedFrom":[subQ1,subQ0]});Q11=makeQuery(id+"F10.imprint","IMPRINT",FACE,{"disambiguationData":[TD([[makeQuery(id+"F10.imprint","IMPRINT",EDGE,{"disambiguationData":[TD([[subQ2,-1.0]])],"derivedFrom":subQ1}),1.0]])]});}
            var Q12;
            {var subQ0=sQuery(id+"F10.wireOp",EDGE,"E35.3");var subQ1=sQuery(id+"F10.wireOp",EDGE,"E35.0");var subQ2=makeQuery(id+"F10.imprint","INTERSECT",VERTEX,{"derivedFrom":[subQ1,subQ0]});Q12=makeQuery(id+"F10.imprint","IMPRINT",FACE,{"disambiguationData":[TD([[makeQuery(id+"F10.imprint","IMPRINT",EDGE,{"disambiguationData":[TD([[subQ2,1.0]])],"derivedFrom":subQ1}),1.0]])]});}
            var Q13;
            {var subQ7=sQuery(id+"F10.wireOp",EDGE,"E35.3");var subQ8=sQuery(id+"F10.wireOp",EDGE,"E35.0");var subQ9=makeQuery(id+"F10.imprint","INTERSECT",VERTEX,{"derivedFrom":[subQ8,subQ7]});Q13=makeQuery(id+"F10.imprint","IMPRINT",FACE,{"disambiguationData":[TD([[makeQuery(id+"F10.imprint","IMPRINT",EDGE,{"disambiguationData":[TD([[subQ9,1.0]])],"derivedFrom":subQ8}),-1.0]])]});}
            var Q14;
            {var subQ0=sQuery(id+"F10.wireOp",EDGE,"E34.3");Q14=makeQuery(id+"F10.imprint","IMPRINT",FACE,{"disambiguationData":[TD([[makeQuery(id+"F10.imprint","IMPRINT",EDGE,{"derivedFrom":subQ0}),-1.0]])]});}
            var Q15;
            {var subQ0=sQuery(id+"F10.wireOp",EDGE,"E39");var subQ1=sQuery(id+"F10.wireOp",EDGE,"E35.0");var subQ2=makeQuery(id+"F10.imprint","INTERSECT",VERTEX,{"derivedFrom":[subQ1,subQ0]});Q15=makeQuery(id+"F10.imprint","IMPRINT",FACE,{"disambiguationData":[TD([[makeQuery(id+"F10.imprint","IMPRINT",EDGE,{"disambiguationData":[TD([[subQ2,-1.0]])],"derivedFrom":subQ1}),-1.0]])]});}
            var Q16;
            {var subQ0=sQuery(id+"F10.wireOp",EDGE,"E35.1");var subQ1=sQuery(id+"F10.wireOp",EDGE,"E35.0");var subQ2=makeQuery(id+"F10.imprint","INTERSECT",VERTEX,{"derivedFrom":[subQ1,subQ0]});Q16=makeQuery(id+"F10.imprint","IMPRINT",FACE,{"disambiguationData":[TD([[makeQuery(id+"F10.imprint","IMPRINT",EDGE,{"disambiguationData":[TD([[subQ2,-1.0]])],"derivedFrom":subQ1}),1.0]])]});}
            var Q17;
            {var subQ7=sQuery(id+"F10.wireOp",EDGE,"E35.0");var subQ9=sQuery(id+"F10.wireOp",EDGE,"E35.1");var subQ10=makeQuery(id+"F10.imprint","INTERSECT",VERTEX,{"derivedFrom":[subQ7,subQ9]});Q17=makeQuery(id+"F10.imprint","IMPRINT",FACE,{"disambiguationData":[TD([[makeQuery(id+"F10.imprint","IMPRINT",EDGE,{"disambiguationData":[TD([[subQ10,-1.0]])],"derivedFrom":subQ7}),-1.0]])]});}
            extrude(context, id + "F19", {"entities" : qUnion([Q0, Q1, Q2, Q3, Q4, Q5, Q6, Q7, Q8, Q9, Q10, Q11, Q12, Q13, Q14, Q15, Q16, Q17]), "depth" : .5 * mm});
        }
        {
            var Q0;
            Q0=makeQuery(id+"F5.imprint","IMPRINT",FACE,{"disambiguationData":[TD([[makeQuery(id+"F5.imprint","IMPRINT",EDGE,{"derivedFrom":sQuery(id+"F5.wireOp",EDGE,"E32")}),1.0]])]});
            extrude(context, id + "F20", {"entities" : qUnion([Q0]), "depth" : 1.25 * mm});
        }
    });
